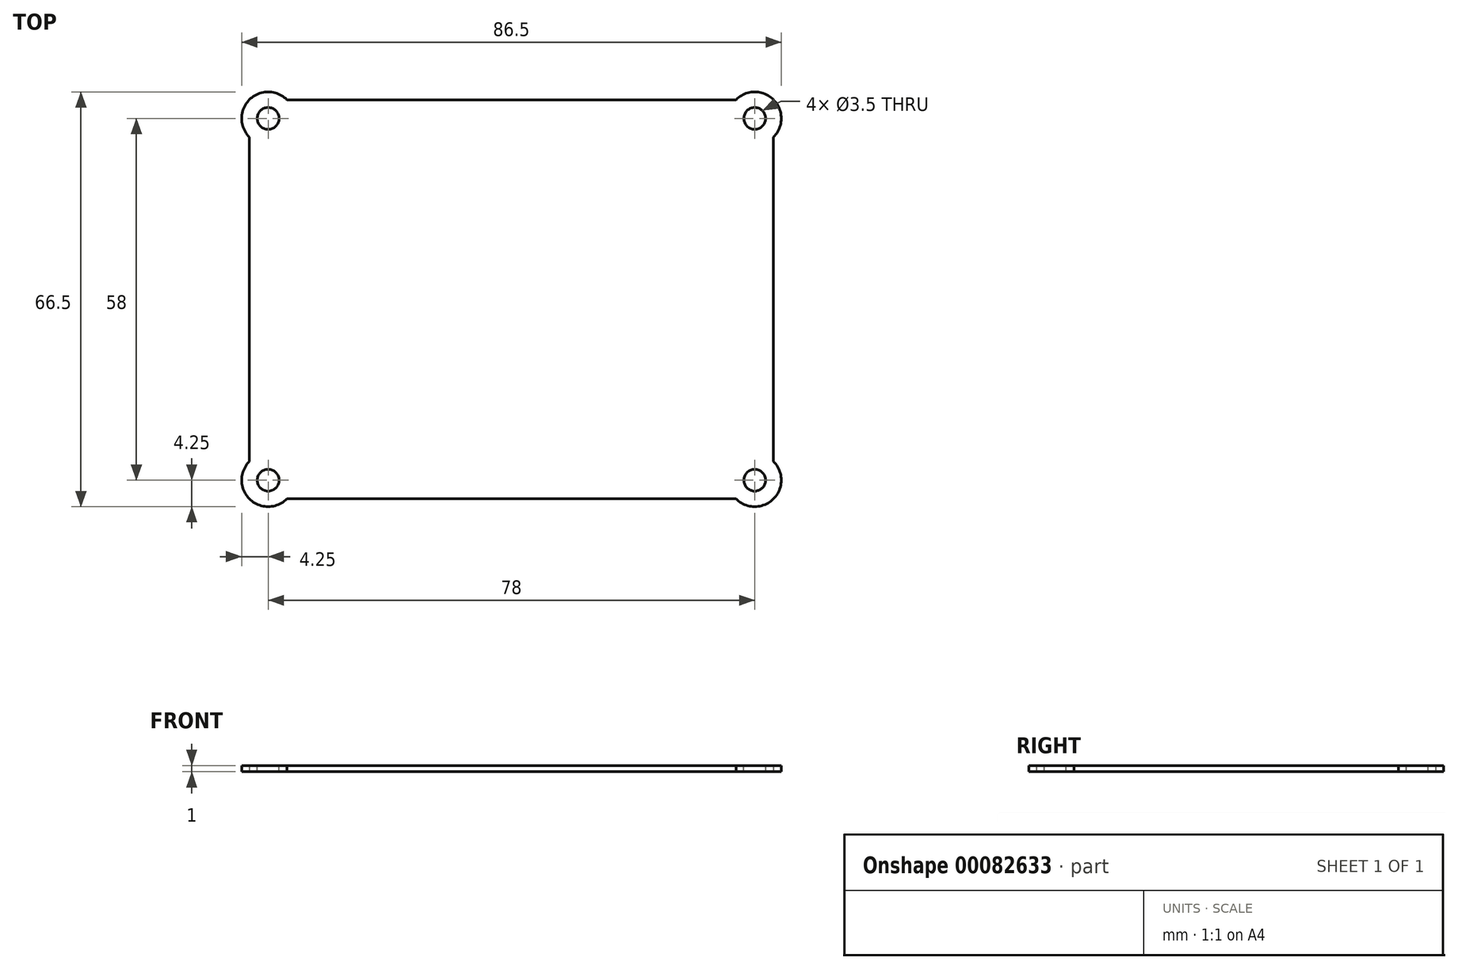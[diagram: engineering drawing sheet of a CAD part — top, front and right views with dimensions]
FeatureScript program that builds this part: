
annotation { "Feature Type Name" : "Feature", "Feature Type Description" : "" }
export const myFeature = defineFeature(function(context is Context, id is Id, definition is map)
    precondition{}
    {
        {
            var Q0;
            Q0=qCreatedBy(makeId("Top.planeOp"),FACE);
            var sketch = newSketch(context, id + "F0", { "sketchPlane" : qUnion([Q0])});
            skLineSegment(sketch, "E0.bottom", {"start": v(42, -32) * mm, "end": v(-42, -32) * mm});
            skLineSegment(sketch, "E0.top", {"start": v(42, 32) * mm, "end": v(-42, 32) * mm});
            skLineSegment(sketch, "E0.left", {"start": v(42, -32) * mm, "end": v(42, 32) * mm});
            skLineSegment(sketch, "E0.right", {"start": v(-42, -32) * mm, "end": v(-42, 32) * mm});
            skPoint(sketch, "E0.middle", {"position": v(0, 0) * mm});
            skSolve(sketch);
        }
        {
            var Q0;
            Q0=makeQuery(id+"F0.imprint","IMPRINT",FACE,{"disambiguationData":[TD([[makeQuery(id+"F0.imprint","IMPRINT",EDGE,{"derivedFrom":sQuery(id+"F0.wireOp",EDGE,"E0.bottom")}),-1.0]])]});
            extrude(context, id + "F1", {"entities" : qUnion([Q0]), "depth" : 1 * mm, "offsetDistance" : 25 * mm});
        }
        {
            var Q0;
            Q0=makeQuery(id+"F1.opExtrude","CAP_FACE",FACE,{"disambiguationData":[OSD([sQuery(id+"F0.wireOp",EDGE,"E0.bottom"),sQuery(id+"F0.wireOp",EDGE,"E0.top"),sQuery(id+"F0.wireOp",EDGE,"E0.left"),sQuery(id+"F0.wireOp",EDGE,"E0.right")])],"isStart":true});
            var sketch = newSketch(context, id + "F2", { "sketchPlane" : qUnion([Q0])});
            skLineSegment(sketch, "E1", {"start": v(0, 32) * mm, "end": v(0, -32) * mm, "construction": true});
            skCircle(sketch, "E2", {"center": v(-39, 29) * mm, "radius": 4.25 * mm});
            skLineSegment(sketch, "E3", {"start": v(-42, 0) * mm, "end": v(42, 0) * mm, "construction": true});
            skCircle(sketch, "E4.MirrorC", {"center": v(-39, -29) * mm, "radius": 4.25 * mm});
            skCircle(sketch, "E5.MirrorC", {"center": v(39, -29) * mm, "radius": 4.25 * mm});
            skCircle(sketch, "E6.MirrorC", {"center": v(39, 29) * mm, "radius": 4.25 * mm});
            skSolve(sketch);
        }
        {
            var Q0;
            Q0=qSketchRegion(id+"F2",true);
            extrude(context, id + "F3", {"entities" : qUnion([Q0]), "operationType" : NewBodyOperationType.ADD, "oppositeDirection" : true, "depth" : 1 * mm, "offsetDistance" : 25 * mm});
        }
        {
            var Q0;
            Q0=makeQuery(id+"F3.boolean.opBoolean","MERGE",FACE,{"derivedFrom":[makeQuery(id+"F1.opExtrude","CAP_FACE",FACE,{"disambiguationData":[OSD([sQuery(id+"F0.wireOp",EDGE,"E0.bottom"),sQuery(id+"F0.wireOp",EDGE,"E0.top"),sQuery(id+"F0.wireOp",EDGE,"E0.left"),sQuery(id+"F0.wireOp",EDGE,"E0.right")])],"isStart":false}),makeQuery(id+"F3.opExtrude","CAP_FACE",FACE,{"disambiguationData":[OSD([sQuery(id+"F2.wireOp",EDGE,"E2")])],"isStart":false}),makeQuery(id+"F3.opExtrude","CAP_FACE",FACE,{"disambiguationData":[OSD([sQuery(id+"F2.wireOp",EDGE,"E4.MirrorC")])],"isStart":false}),makeQuery(id+"F3.opExtrude","CAP_FACE",FACE,{"disambiguationData":[OSD([sQuery(id+"F2.wireOp",EDGE,"E5.MirrorC")])],"isStart":false}),makeQuery(id+"F3.opExtrude","CAP_FACE",FACE,{"disambiguationData":[OSD([sQuery(id+"F2.wireOp",EDGE,"E6.MirrorC")])],"isStart":false})]});
            var sketch = newSketch(context, id + "F4", { "sketchPlane" : qUnion([Q0])});
            skCircle(sketch, "E7", {"center": v(-39, 29) * mm, "radius": 1.75 * mm});
            skCircle(sketch, "E8", {"center": v(39, 29) * mm, "radius": 1.75 * mm});
            skCircle(sketch, "E9", {"center": v(-39, -29) * mm, "radius": 1.75 * mm});
            skCircle(sketch, "E10", {"center": v(39, -29) * mm, "radius": 1.75 * mm});
            skSolve(sketch);
        }
        {
            var Q0;
            Q0=qSketchRegion(id+"F4",true);
            extrude(context, id + "F5", {"entities" : qUnion([Q0]), "operationType" : NewBodyOperationType.REMOVE, "oppositeDirection" : true, "depth" : 40 * mm});
        }
    });
